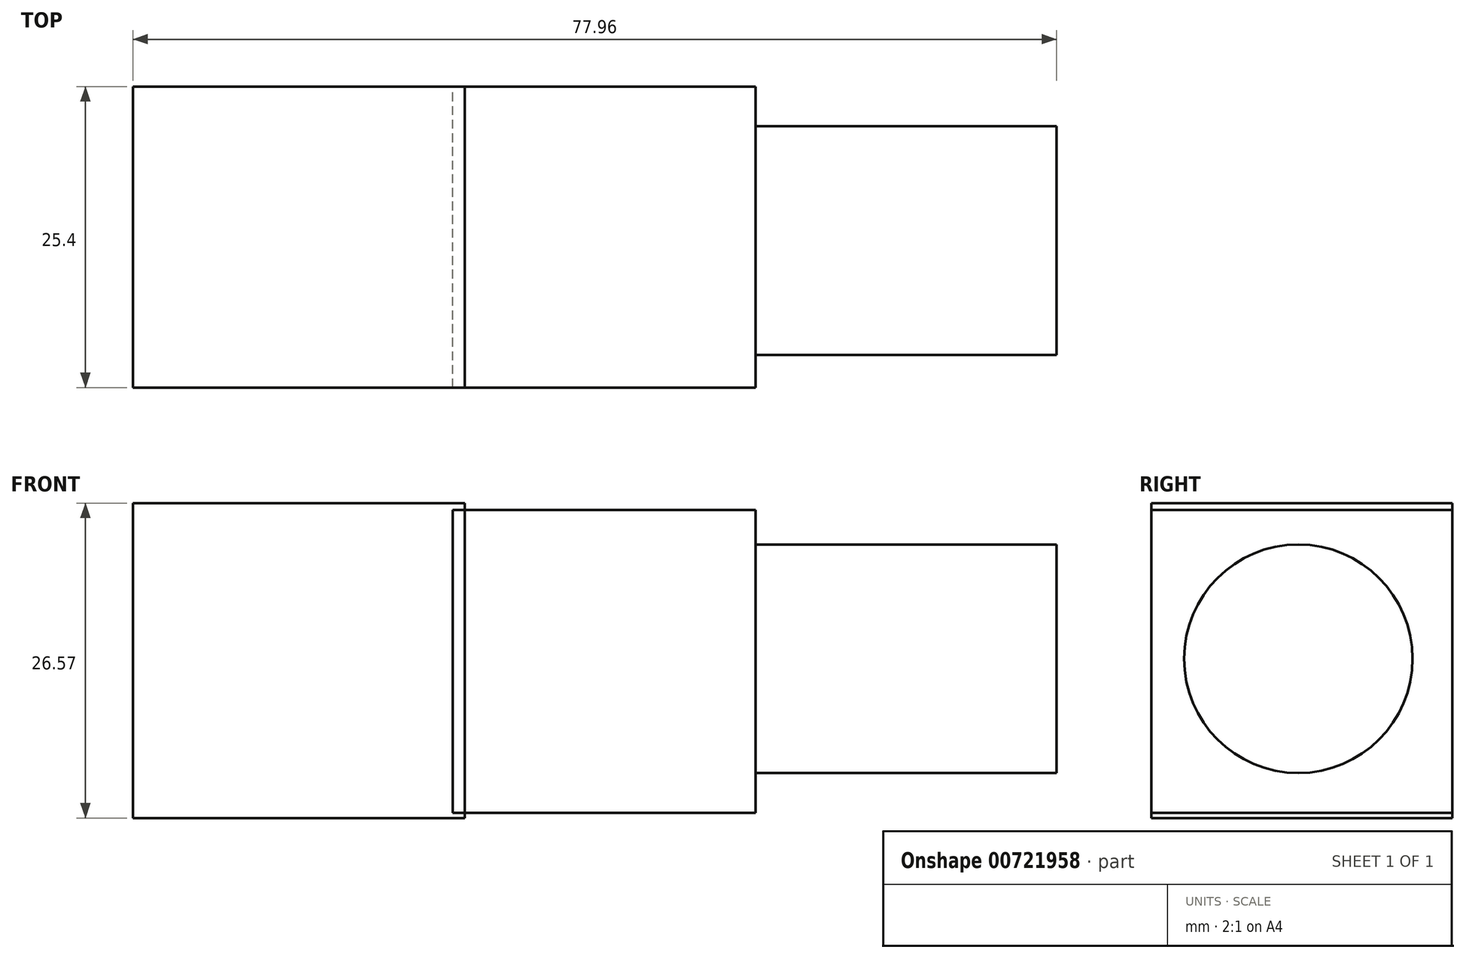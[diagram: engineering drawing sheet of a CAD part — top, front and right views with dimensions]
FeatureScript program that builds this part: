
annotation { "Feature Type Name" : "Feature", "Feature Type Description" : "" }
export const myFeature = defineFeature(function(context is Context, id is Id, definition is map)
    precondition{}
    {
        {
            var Q0;
            Q0=qCreatedBy(makeId("Front.planeOp"),FACE);
            var sketch = newSketch(context, id + "F0", { "sketchPlane" : qUnion([Q0])});
            skLineSegment(sketch, "E0.bottom", {"start": v(0, 0) * mm, "end": v(25.55, 0) * mm});
            skLineSegment(sketch, "E0.top", {"start": v(0, 25.55) * mm, "end": v(25.55, 25.55) * mm});
            skLineSegment(sketch, "E0.left", {"start": v(0, 0) * mm, "end": v(0, 25.55) * mm});
            skLineSegment(sketch, "E0.right", {"start": v(25.55, 0) * mm, "end": v(25.55, 25.55) * mm});
            skLineSegment(sketch, "E1.bottom", {"start": v(0, 25.55) * mm, "end": v(-26.43, 25.55) * mm});
            skLineSegment(sketch, "E1.top", {"start": v(0, 25.55) * mm, "end": v(-26.43, 25.55) * mm});
            skLineSegment(sketch, "E1.left", {"start": v(0, 25.55) * mm, "end": v(0, 25.55) * mm});
            skLineSegment(sketch, "E1.right", {"start": v(-26.43, 25.55) * mm, "end": v(-26.43, 25.55) * mm});
            skLineSegment(sketch, "E2.bottom", {"start": v(-27.01, 26.13) * mm, "end": v(1.02, 26.13) * mm});
            skLineSegment(sketch, "E2.top", {"start": v(-27.01, -0.44) * mm, "end": v(1.02, -0.44) * mm});
            skLineSegment(sketch, "E2.left", {"start": v(-27.01, 26.13) * mm, "end": v(-27.01, -0.44) * mm});
            skLineSegment(sketch, "E2.right", {"start": v(1.02, 26.13) * mm, "end": v(1.02, -0.44) * mm});
            skSolve(sketch);
        }
        {
            var Q0;
            {var subQ1=sQuery(id+"F0.wireOp",EDGE,"E0.left");Q0=makeQuery(id+"F0.imprint","IMPRINT",FACE,{"disambiguationData":[TD([[makeQuery(id+"F0.imprint","IMPRINT",EDGE,{"derivedFrom":subQ1}),1.0]])]});}
            var Q1;
            {var subQ0=sQuery(id+"F0.wireOp",EDGE,"E0.right");Q1=makeQuery(id+"F0.imprint","IMPRINT",FACE,{"disambiguationData":[TD([[makeQuery(id+"F0.imprint","IMPRINT",EDGE,{"derivedFrom":subQ0}),1.0]])]});}
            extrude(context, id + "F1", {"entities" : qUnion([Q0, Q1]), "depth" : 25.4 * mm, "offsetDistance" : 25.4 * mm});
        }
        {
            var Q0;
            Q0=makeQuery(id+"F1.opExtrude","SWEPT_FACE",FACE,{"disambiguationData":[OSD([sQuery(id+"F0.wireOp",EDGE,"E0.right")])]});
            var sketch = newSketch(context, id + "F2", { "sketchPlane" : qUnion([Q0])});
            skCircle(sketch, "E3", {"center": v(-13, 13) * mm, "radius": 9.64 * mm});
            skSolve(sketch);
        }
        {
            var Q0;
            Q0=makeQuery(id+"F2.imprint","IMPRINT",FACE,{"disambiguationData":[TD([[makeQuery(id+"F2.imprint","IMPRINT",EDGE,{"derivedFrom":sQuery(id+"F2.wireOp",EDGE,"E3")}),1.0]])]});
            extrude(context, id + "F3", {"entities" : qUnion([Q0]), "operationType" : NewBodyOperationType.ADD, "depth" : 25.4 * mm, "offsetDistance" : 25.4 * mm});
        }
    });
